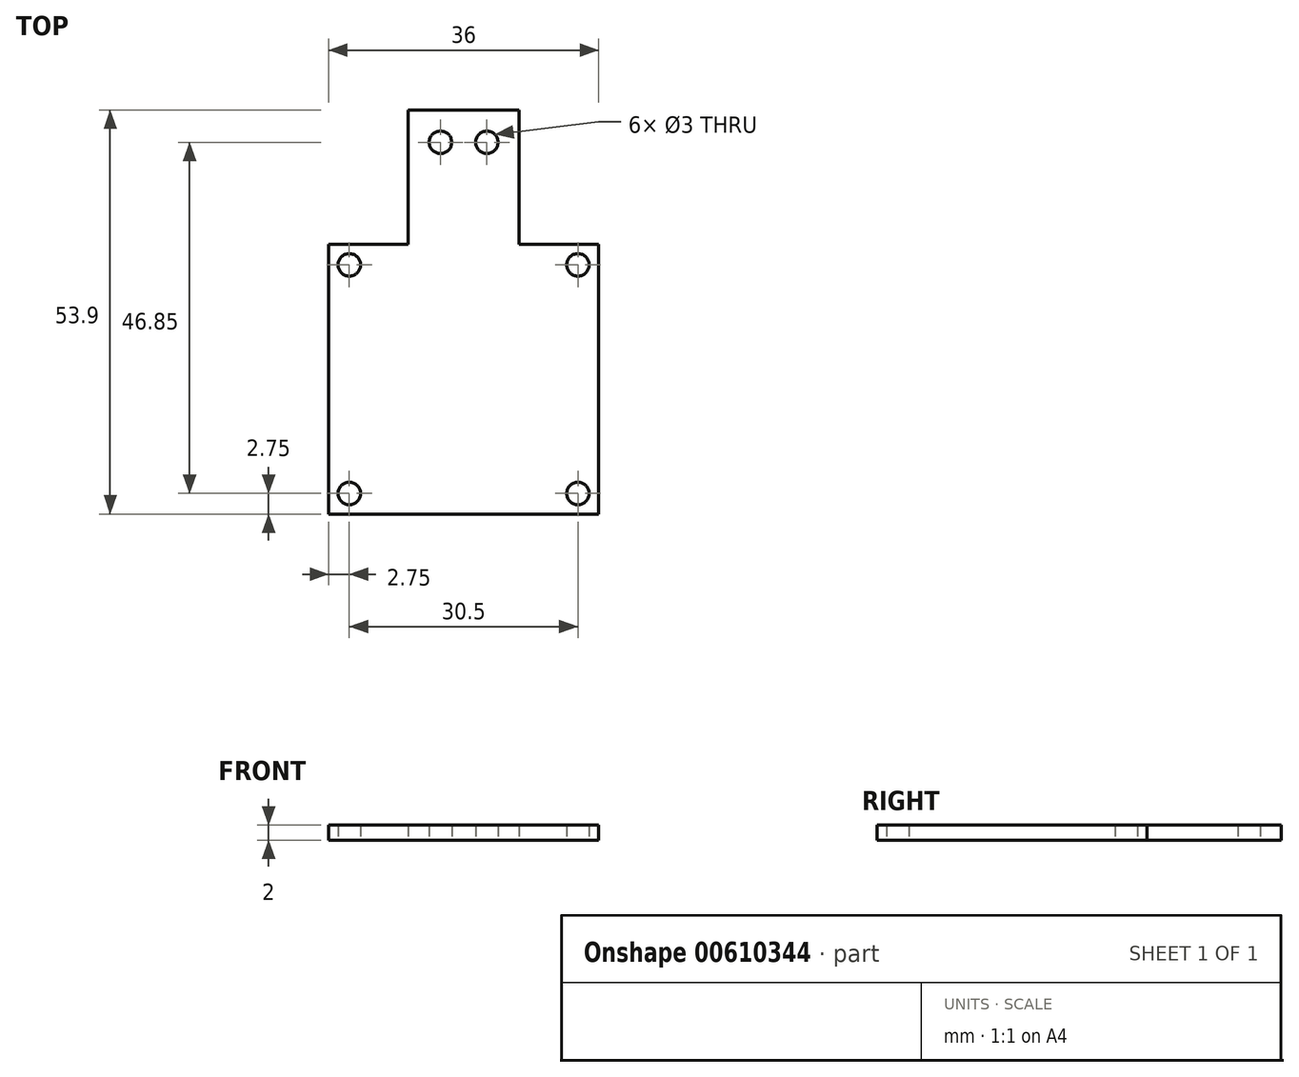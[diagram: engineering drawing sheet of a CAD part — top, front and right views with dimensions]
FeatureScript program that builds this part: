
annotation { "Feature Type Name" : "Feature", "Feature Type Description" : "" }
export const myFeature = defineFeature(function(context is Context, id is Id, definition is map)
    precondition{}
    {
        {
            var Q0;
            Q0=qCreatedBy(makeId("Top.planeOp"),FACE);
            var sketch = newSketch(context, id + "F0", { "sketchPlane" : qUnion([Q0])});
            skLineSegment(sketch, "E0", {"start": v(-18, 18) * mm, "end": v(-18, -18) * mm});
            skLineSegment(sketch, "E1", {"start": v(18, -18) * mm, "end": v(18, 18) * mm});
            skLineSegment(sketch, "E2", {"start": v(18, 18) * mm, "end": v(-18, 18) * mm});
            skLineSegment(sketch, "E3", {"start": v(-18, -18) * mm, "end": v(18, -18) * mm});
            skLineSegment(sketch, "E4", {"start": v(-7.4, 18) * mm, "end": v(-7.4, 35.9) * mm});
            skLineSegment(sketch, "E5", {"start": v(-7.4, 35.9) * mm, "end": v(7.4, 35.9) * mm});
            skLineSegment(sketch, "E6", {"start": v(7.4, 35.9) * mm, "end": v(7.4, 18) * mm});
            skCircle(sketch, "E7", {"center": v(-15.25, 15.25) * mm, "radius": 1.5 * mm});
            skCircle(sketch, "E8", {"center": v(-15.25, -15.25) * mm, "radius": 1.5 * mm});
            skCircle(sketch, "E9.MirrorC", {"center": v(15.25, -15.25) * mm, "radius": 1.5 * mm});
            skCircle(sketch, "E10.MirrorC", {"center": v(15.25, 15.25) * mm, "radius": 1.5 * mm});
            skCircle(sketch, "E11", {"center": v(-3.09, 31.6) * mm, "radius": 1.5 * mm});
            skCircle(sketch, "E12", {"center": v(3.1, 31.6) * mm, "radius": 1.5 * mm});
            skSolve(sketch);
        }
        {
            var Q0;
            Q0 = qSketchRegion(id + "F0", true);
            extrude(context, id + "F1", {"entities" : qUnion([Q0]), "depth" : 2 * mm, "offsetDistance" : 25 * mm});
        }
    });
